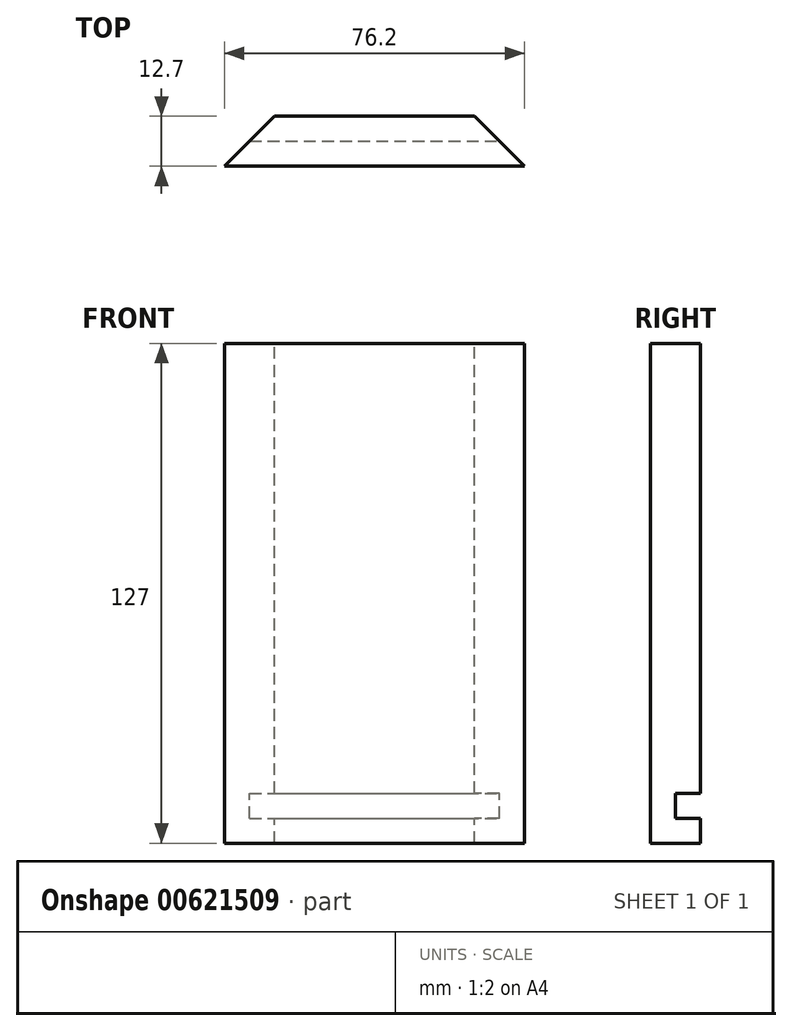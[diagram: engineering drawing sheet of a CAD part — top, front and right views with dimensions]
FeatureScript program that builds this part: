
annotation { "Feature Type Name" : "Feature", "Feature Type Description" : "" }
export const myFeature = defineFeature(function(context is Context, id is Id, definition is map)
    precondition{}
    {
        {
            var Q0;
            Q0=qCreatedBy(makeId("Top.planeOp"),FACE);
            var sketch = newSketch(context, id + "F0", { "sketchPlane" : qUnion([Q0])});
            skLineSegment(sketch, "E0.bottom", {"start": v(-38.1, -12.7) * mm, "end": v(38.1, -12.7) * mm});
            skLineSegment(sketch, "E0.top", {"start": v(-38.1, -25.4) * mm, "end": v(38.1, -25.4) * mm});
            skLineSegment(sketch, "E0.left", {"start": v(-38.1, -12.7) * mm, "end": v(-38.1, -25.4) * mm});
            skLineSegment(sketch, "E0.right", {"start": v(38.1, -12.7) * mm, "end": v(38.1, -25.4) * mm});
            skSolve(sketch);
        }
        {
            var Q0;
            Q0=makeQuery(id+"F0.imprint","IMPRINT",FACE,{"disambiguationData":[TD([[makeQuery(id+"F0.imprint","IMPRINT",EDGE,{"derivedFrom":sQuery(id+"F0.wireOp",EDGE,"E0.bottom")}),-1.0]])]});
            extrude(context, id + "F1", {"entities" : qUnion([Q0]), "depth" : 127 * mm, "offsetDistance" : 25.4 * mm});
        }
        {
            var Q0;
            Q0=makeQuery(id+"F1.opExtrude","SWEPT_FACE",FACE,{"disambiguationData":[OSD([sQuery(id+"F0.wireOp",EDGE,"E0.right")])]});
            var sketch = newSketch(context, id + "F2", { "sketchPlane" : qUnion([Q0])});
            skLineSegment(sketch, "E1.bottom", {"start": v(-6.35, 12.7) * mm, "end": v(-19.05, 12.7) * mm});
            skLineSegment(sketch, "E1.top", {"start": v(-6.35, 6.35) * mm, "end": v(-19.05, 6.35) * mm});
            skLineSegment(sketch, "E1.left", {"start": v(-6.35, 12.7) * mm, "end": v(-6.35, 6.35) * mm});
            skLineSegment(sketch, "E1.right", {"start": v(-19.05, 12.7) * mm, "end": v(-19.05, 6.35) * mm});
            skSolve(sketch);
        }
        {
            var Q0;
            {var subQ0=sQuery(id+"F2.wireOp",EDGE,"E1.right");Q0=makeQuery(id+"F2.imprint","IMPRINT",FACE,{"disambiguationData":[TD([[makeQuery(id+"F2.imprint","IMPRINT",EDGE,{"derivedFrom":subQ0}),1.0]])]});}
            extrude(context, id + "F3", {"entities" : qUnion([Q0]), "operationType" : NewBodyOperationType.REMOVE, "endBound" : BoundingType.UP_TO_NEXT, "oppositeDirection" : true, "depth" : 25.4 * mm, "offsetDistance" : 25.4 * mm});
        }
        {
            var Q0;
            Q0=makeQuery(id+"F1.opExtrude","CAP_FACE",FACE,{"disambiguationData":[OSD([sQuery(id+"F0.wireOp",EDGE,"E0.bottom"),sQuery(id+"F0.wireOp",EDGE,"E0.top"),sQuery(id+"F0.wireOp",EDGE,"E0.left"),sQuery(id+"F0.wireOp",EDGE,"E0.right")])],"isStart":false});
            var sketch = newSketch(context, id + "F4", { "sketchPlane" : qUnion([Q0])});
            skLineSegment(sketch, "E2", {"start": v(-38.1, -25.4) * mm, "end": v(-25.4, -12.7) * mm});
            skLineSegment(sketch, "E3", {"start": v(-25.4, -12.7) * mm, "end": v(-38.1, -12.7) * mm});
            skLineSegment(sketch, "E4", {"start": v(-38.1, -12.7) * mm, "end": v(-38.1, -25.4) * mm});
            skLineSegment(sketch, "E5", {"start": v(38.1, -25.4) * mm, "end": v(25.4, -12.7) * mm});
            skLineSegment(sketch, "E6", {"start": v(25.4, -12.7) * mm, "end": v(38.1, -12.7) * mm});
            skLineSegment(sketch, "E7", {"start": v(38.1, -12.7) * mm, "end": v(38.1, -25.4) * mm});
            skSolve(sketch);
        }
        {
            var Q0;
            Q0=makeQuery(id+"F4.imprint","IMPRINT",FACE,{"disambiguationData":[TD([[makeQuery(id+"F4.imprint","IMPRINT",EDGE,{"derivedFrom":sQuery(id+"F4.wireOp",EDGE,"E2")}),1.0]])]});
            var Q1;
            Q1=makeQuery(id+"F4.imprint","IMPRINT",FACE,{"disambiguationData":[TD([[makeQuery(id+"F4.imprint","IMPRINT",EDGE,{"derivedFrom":sQuery(id+"F4.wireOp",EDGE,"E5")}),-1.0]])]});
            extrude(context, id + "F5", {"entities" : qUnion([Q0, Q1]), "operationType" : NewBodyOperationType.REMOVE, "endBound" : BoundingType.THROUGH_ALL, "oppositeDirection" : true, "depth" : 25.4 * mm, "offsetDistance" : 25.4 * mm});
        }
    });
